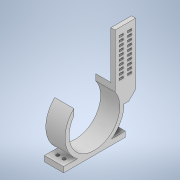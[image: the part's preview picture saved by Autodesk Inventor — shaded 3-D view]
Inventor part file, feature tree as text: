
AUTODESK INVENTOR PART (.ipt)
format: ipt  version: 2020 (Build 240168000, 168)  size: 251,904 bytes
history: native  units: in
note: dims shown in document units (in); Inventor stores cm internally (conversion verified against a paired STEP export)
features: extrude x6, sketch x5, chamfer x1, pattern_linear x1
ambient origin geometry x8: Origin, YZ Plane, XZ Plane, XY Plane, X Axis, Y Axis, Z Axis, Center Point
bodies: Solid1 (feature_tree)
feature tree (13):
  extrude  "Extrusion1"  Depth=2.15in
  extrude  "Extrusion2"  Depth=0.7in TaperAngle=0.0deg
  extrude  "Extrusion3"  Depth=0.75in
  extrude  "Extrusion4"  Depth=0.15in TaperAngle=0.0deg
  extrude  "Extrusion5"  Depth=2.25in
  chamfer  "Chamfer1"  Distance=1.125in
  extrude  "Extrusion6"  Depth=0.15in
  pattern_linear  "Rectangular Pattern1"  Spacing1=0.118in  [1 undecoded]
  sketch  "Sketch1"  dims[d0=1.85in d1=2.15in]
  sketch  "Sketch2"  dims[d2=0.2in d3=0.7in d4=0.0in]
  sketch  "Sketch4"  dims[d5=1.5in d6=0.75in]
  sketch  "Sketch5"  dims[d7=2.5in d8=0.15in d9=0.0in]
  sketch  "Sketch6"  dims[d10=0.0in d11=2.25in d12=1.125in d13=0.118in d14=0.118in d15=0.0in d16=0.25in d17=0.25in d18=0.2333in d19=0.25in d20=0.0in d21=0.15in d22=0.3in d23=0.25in d24=0.0in d25=0.25in d26=0.0in d27=0.15in d28=0.0in d29=0.25in d30=0.125in d31=45.0deg d32=0.118in d33=0.118in d34=0.2333in d35=1.75in d36=0.2333in d37=0.065in d38=0.25in d39=0.15in d40=0.15in d41=0.15in d42=0.15in d43=0.15in d44=0.25in d45=0.0in d46=3.937in d48=0.15in]
note: 1 required parameter value undecoded (feature->parameter linkage not recoverable at this tier; creation-order binding heuristic only, values carry confidence <= 0.55)
